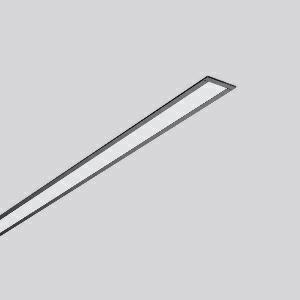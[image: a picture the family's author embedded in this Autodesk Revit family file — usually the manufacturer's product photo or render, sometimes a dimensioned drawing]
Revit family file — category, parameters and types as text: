
# Revit family: less_is_more_27_312178_003_76_7076
name_source: partatom
category: Lighting Fixtures
units: mm (PartAtom-declared; Revit-internal decimal feet)

## family parameters
Cut with Voids When Loaded = No
Host = Face
Light Source = No
Part Type = Normal
Room Calculation Point = No
Round Connector Dimension = Use Diameter
Shared = No

## types (1)
- LESS IS MORE 27 (1 x LED Modul 830, 2400 lm, 3000)
    Apparent Load = 43 VA
    CIE Flux Codes = 48 79 96 100 100
    Color Rendering = 80
    Color Temperature = 3000
    Default Elevation = 1800 mm
    Description = Series: LESS IS MORE 27
Recessed ceiling and wall luminaire with slim design. Housing: extruded aluminium profile, powder-coated. End cap aluminium powder-coated. Diffuser made of non-yellowing plastic (PMMA), opal. Suitable for Recessed ceiling mounting, wall (recessed). External driver with connecting cable. 
Colour: deep black, matt (RAL 9005)
Length: 1514 mm
Width: 38 mm
Height: 2 mm
Cut-out length: 1506 mm
Cut-out width: 30 mm
Recess height: 45-60 mm
Luminaire: recess height: 37 mm
Lamp: LED
Socket: without socket
Colour temperature: 3000K
Colour rendering index (CRI): 82
System power: 43 W
Rated luminous flux: 2400 lm
Luminous efficiency: 56 lm/W
Control gear: Voltage converter, DALI dim.
Protection class: II
Type of protection: IP 20
    Height = 0 mm  [stored 0 ft]
    Lamp = 1 x LED Modul 830
    Lamp Light Flux = 2400 lm
    Lamp count = 1
    Length = 1514 mm
    Lifetime = 50000 h
    Luminous efficacy = 56 lm/W
    Manufacturer = RZB
    ModVariant = No
    Model = 312178.003.76
    Mounting Place = Ceiling, Wall
    Mounting Type = Recessed
    Number of Poles = 1
    OnlyDefault = Yes
    Power Factor = 1
    Product Name = LESS IS MORE 27
    Product group = Recessed LED linear luminaires
    ProductGroupID = 407
    Protection Class = Protection class II
    Protection Degree = IP 20
    RLX_Detail_Level = 1
    RLX_Emergency_Light_Flux = 0 lm
    RLX_Emergency_Type = 0
    RLX_Emergency_Type_DB = No
    RlxData = <blob elided: 26145 chars, md5=8c3a77dc>
    Socket = socket
    Standby Power = 0 W
    System Light Flux = 2400 lm
    System Power = 43 W
    Type Comments = Product without accessories
    Type Image = 312176.003.jpg
    URL = http://relux.com
    VarID = ---
    Voltage = 230 V
    Voltage Range = 220-240 V
    Weight = 0.00 kg
    Width = 38 mm

note: [stored X ft] marks values corroborated as IEEE doubles in the binary element streams (Revit-internal decimal feet)

## geometry (parser evidence)
native form markers: Blend x4, Sweep x11
no freeform markers — native parametric forms only
